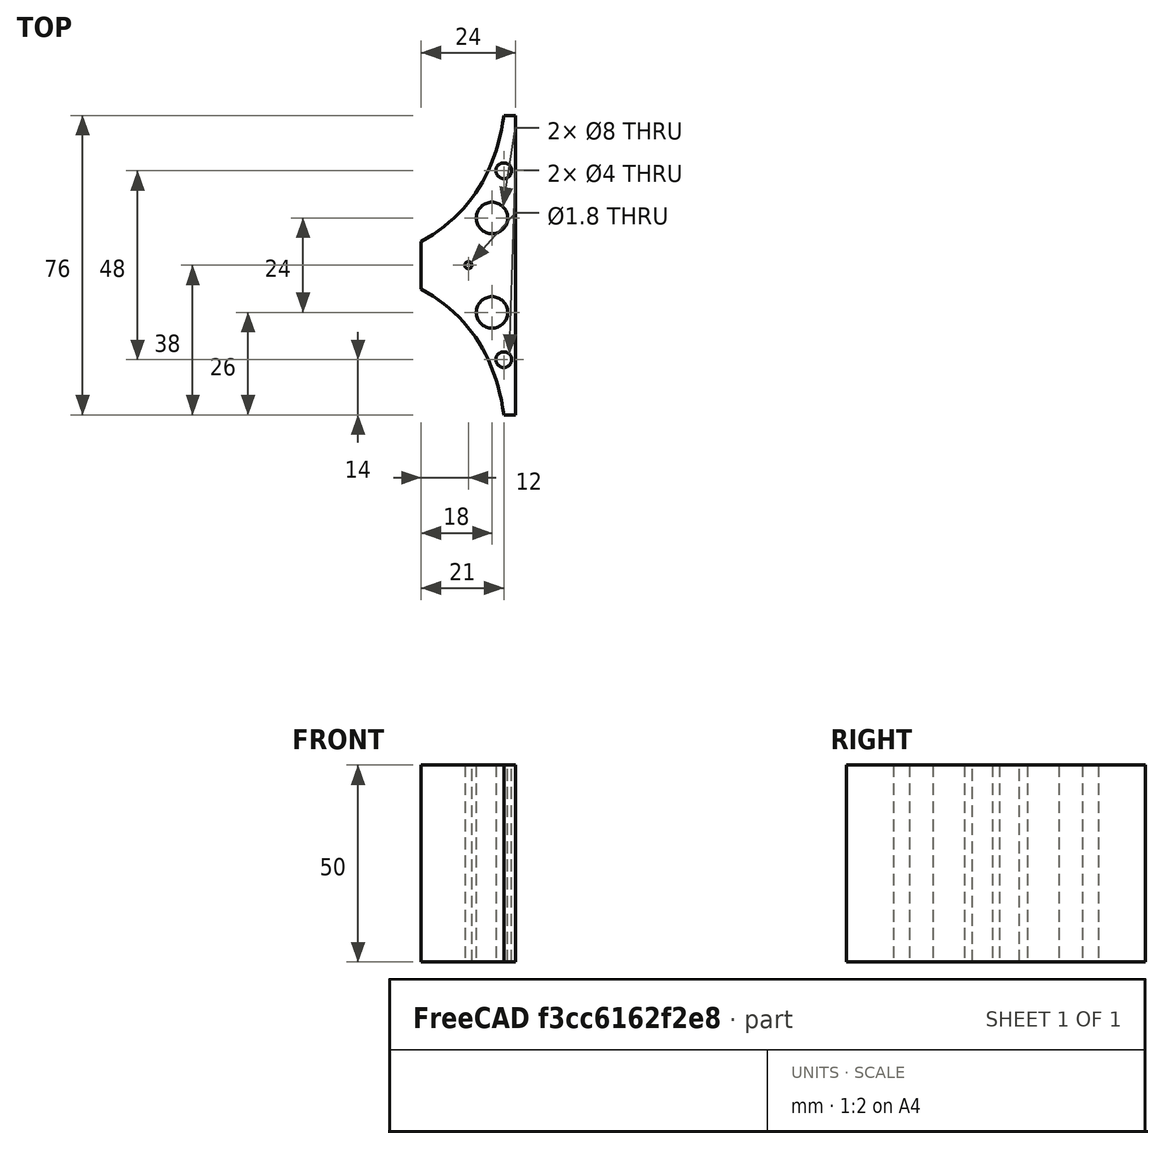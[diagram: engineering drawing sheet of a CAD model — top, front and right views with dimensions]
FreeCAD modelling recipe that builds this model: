
FCSTD DOCUMENT  (FreeCAD 0.20R0.20.2)
Label: 0.005
License: All rights reserved
LicenseURL: http://en.wikipedia.org/wiki/All_rights_reserved
objects: Sketcher::SketchObject×2, Part::Extrusion×1
note: 3 computed .brp shape members not serialized (recipe doc carries the construction recipe); baked Part::Feature solids carry a one-line shape summary decoded from their .brp

FEATURE [Sketcher::SketchObject] Sketch
  FullyConstrained = true
  sketch-geometry (23):
    g0: Circle CenterX=0 CenterY=0 CenterZ=0 NormalX=0 NormalY=0 NormalZ=1 AngleXU=0 Radius=0.9
    g1: LineSegment StartX=12 StartY=0 StartZ=0 EndX=12 EndY=38 EndZ=0
    g2: LineSegment StartX=12 StartY=0 StartZ=0 EndX=12 EndY=-38 EndZ=0
    g3: LineSegment StartX=12 StartY=38 StartZ=0 EndX=9 EndY=38 EndZ=0
    g4: LineSegment StartX=12 StartY=-38 StartZ=0 EndX=9 EndY=-38 EndZ=0
    g5: LineSegment StartX=-12 StartY=0 StartZ=0 EndX=-12 EndY=6 EndZ=0
    g6: LineSegment StartX=-12 StartY=0 StartZ=0 EndX=-12 EndY=-6 EndZ=0
    g7: Circle CenterX=-12 CenterY=6 CenterZ=0 NormalX=0 NormalY=0 NormalZ=1 AngleXU=0 Radius=1
    g8: Circle CenterX=6 CenterY=16 CenterZ=0 NormalX=0 NormalY=0 NormalZ=1 AngleXU=0 Radius=1
    g9: Circle CenterX=9 CenterY=38 CenterZ=0 NormalX=0 NormalY=0 NormalZ=1 AngleXU=0 Radius=1
    g10: BSplineCurve PolesCount=3 KnotsCount=2 Degree=2 IsPeriodic=0
    g11: GeomPoint X=-12 Y=6 Z=0
    g12: GeomPoint X=9 Y=38 Z=0
    g13: Circle CenterX=-12 CenterY=-6 CenterZ=0 NormalX=0 NormalY=0 NormalZ=1 AngleXU=0 Radius=1
    g14: Circle CenterX=6 CenterY=-16 CenterZ=0 NormalX=0 NormalY=0 NormalZ=1 AngleXU=0 Radius=1
    g15: Circle CenterX=9 CenterY=-38 CenterZ=0 NormalX=0 NormalY=0 NormalZ=1 AngleXU=0 Radius=1
    g16: BSplineCurve PolesCount=3 KnotsCount=2 Degree=2 IsPeriodic=0
    g17: GeomPoint X=-12 Y=-6 Z=0
    g18: GeomPoint X=9 Y=-38 Z=0
    g19: Circle CenterX=6 CenterY=12 CenterZ=0 NormalX=0 NormalY=0 NormalZ=1 AngleXU=0 Radius=4
    g20: Circle CenterX=6 CenterY=-12 CenterZ=0 NormalX=0 NormalY=0 NormalZ=1 AngleXU=0 Radius=4
    g21: Circle CenterX=9 CenterY=-24 CenterZ=0 NormalX=0 NormalY=0 NormalZ=1 AngleXU=0 Radius=2
    g22: Circle CenterX=9 CenterY=24 CenterZ=0 NormalX=0 NormalY=0 NormalZ=1 AngleXU=0 Radius=2
  constraints (43):
    c: Block(g0)
    c: Vertical(g1)
    c: Distance(g1) = 38
    c: Vertical(g2)
    c: Distance(g2) = 38
    c: Coincident(g3,g1)
    c: Horizontal(g3)
    c: Coincident(g4,g2)
    c: Horizontal(g4)
    c: Distance(g4) = 3
    c: Distance(g3) = 3
    c: Vertical(g5)
    c: Vertical(g6)
    c: Distance(g5) = 6
    c: Distance(g6) = 6
    c: Weight(g7) = 1
    c: Coincident(g10,g5)
    c: Equal(g7,g8)
    c: Equal(g7,g9)
    c: Coincident(g10,g3)
    c: InternalAlignment(g7,g10)
    c: InternalAlignment(g8,g10)
    c: InternalAlignment(g9,g10)
    c: InternalAlignment(g11,g10)
    c: InternalAlignment(g12,g10)
    c: Weight(g13) = 1
    c: Coincident(g16,g6)
    c: Equal(g13,g14)
    c: Equal(g13,g15)
    c: Coincident(g16,g4)
    c: InternalAlignment(g13,g16)
    c: InternalAlignment(g14,g16)
    c: InternalAlignment(g15,g16)
    c: InternalAlignment(g17,g16)
    c: InternalAlignment(g18,g16)
    c: PointOnObject(g8,g19)
    c: PointOnObject(g14,g20)
    c: Block(g19)
    c: Block(g22)
    c: Block(g10)
    c: Block(g16)
    c: Block(g20)
    c: Block(g21)
FEATURE [Part::Extrusion] Extrude  label="nearSwitchHolder"
  Base = -> Sketch
  Dir = (0,0,1)
  DirMode = 2
  FaceMakerClass = Part::FaceMakerBullseye
  LengthFwd = 50
  LengthRev = 0
  Solid = true
  Symmetric = false
FEATURE [Sketcher::SketchObject] Sketch001
  FullyConstrained = true
  MapMode = 3
  Placement = pos=(0,0,0) rot=(1,0,0;1.5708rad)
  Support = -> [Sketch]
  sketch-geometry (4):
    g0: LineSegment StartX=0 StartY=0 StartZ=0 EndX=0.5 EndY=0 EndZ=0
    g1: LineSegment StartX=0 StartY=0 StartZ=0 EndX=0 EndY=50 EndZ=0
    g2: LineSegment StartX=0 StartY=50 StartZ=0 EndX=6.55 EndY=50 EndZ=0
    g3: LineSegment StartX=6.55 StartY=50 StartZ=0 EndX=0.5 EndY=0 EndZ=0
  constraints (11):
    c: Coincident(g0,g-1)
    c: Horizontal(g0)
    c: Distance(g0) = 0.5
    c: Coincident(g1,g0)
    c: Vertical(g1)
    c: Distance(g1) = 50
    c: Coincident(g2,g1)
    c: Horizontal(g2)
    c: Distance(g2) = 6.55
    c: Coincident(g3,g2)
    c: Coincident(g3,g0)
